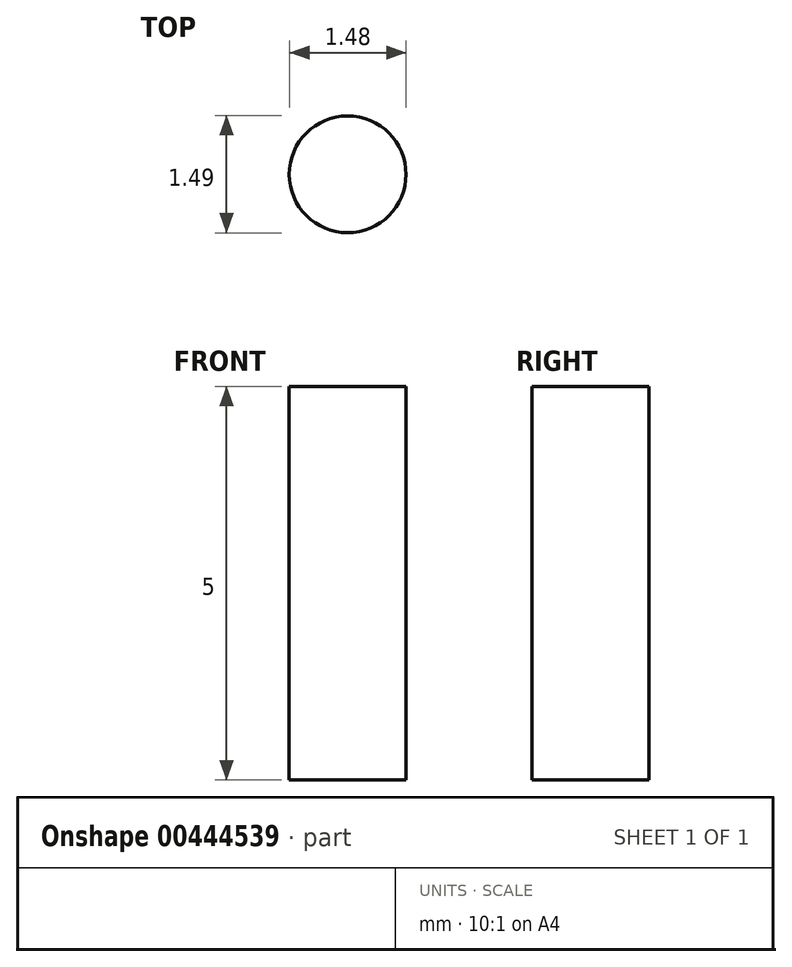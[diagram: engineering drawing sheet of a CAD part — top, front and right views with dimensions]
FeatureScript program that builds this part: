
annotation { "Feature Type Name" : "Feature", "Feature Type Description" : "" }
export const myFeature = defineFeature(function(context is Context, id is Id, definition is map)
    precondition{}
    {
        {
            var Q0;
            Q0=qCreatedBy(makeId("Top.planeOp"),FACE);
            var sketch = newSketch(context, id + "F0", { "sketchPlane" : qUnion([Q0])});
            skLineSegment(sketch, "E0.bottom", {"start": v(-4, 5) * mm, "end": v(4, 5) * mm});
            skLineSegment(sketch, "E0.top", {"start": v(-4, -5) * mm, "end": v(4, -5) * mm});
            skLineSegment(sketch, "E0.left", {"start": v(-5, 4) * mm, "end": v(-5, -4) * mm});
            skLineSegment(sketch, "E0.right", {"start": v(5, 4) * mm, "end": v(5, -4) * mm});
            skPoint(sketch, "E0.middle", {"position": v(0, 0) * mm});
            skPoint(sketch, "E1.visualSharp", {"position": v(-5, 5) * mm});
            skArc(sketch, "E1.filletArc", {"start": v(-4, 5) * mm, "mid": v(-4.7, 4.7) * mm, "end": v(-5, 4) * mm});
            skPoint(sketch, "E2.visualSharp", {"position": v(5, 5) * mm});
            skArc(sketch, "E2.filletArc", {"start": v(5, 4) * mm, "mid": v(4.7, 4.7) * mm, "end": v(4, 5) * mm});
            skPoint(sketch, "E3.visualSharp", {"position": v(5, -5) * mm});
            skArc(sketch, "E3.filletArc", {"start": v(4, -5) * mm, "mid": v(4.7, -4.7) * mm, "end": v(5, -4) * mm});
            skPoint(sketch, "E4.visualSharp", {"position": v(-5, -5) * mm});
            skArc(sketch, "E4.filletArc", {"start": v(-5, -4) * mm, "mid": v(-4.7, -4.7) * mm, "end": v(-4, -5) * mm});
            skSolve(sketch);
        }
        {
            var Q0;
            Q0 = qSketchRegion(id + "F0", true);
            extrude(context, id + "F1", {"entities" : qUnion([Q0]), "depth" : 5 * mm});
        }
        {
            var Q0;
            Q0=makeQuery(id+"F1.opExtrude","CAP_FACE",FACE,{"disambiguationData":[OSD([sQuery(id+"F0.wireOp",EDGE,"E0.bottom"),sQuery(id+"F0.wireOp",EDGE,"E0.top"),sQuery(id+"F0.wireOp",EDGE,"E0.left"),sQuery(id+"F0.wireOp",EDGE,"E0.right"),sQuery(id+"F0.wireOp",EDGE,"E1.filletArc"),sQuery(id+"F0.wireOp",EDGE,"E2.filletArc"),sQuery(id+"F0.wireOp",EDGE,"E3.filletArc"),sQuery(id+"F0.wireOp",EDGE,"E4.filletArc")])],"isStart":false});
            var sketch = newSketch(context, id + "F2", { "sketchPlane" : qUnion([Q0])});
            skCircle(sketch, "E5", {"center": v(-1.87, 1.9) * mm, "radius": 0.74 * mm});
            skCircle(sketch, "E6.MirrorC", {"center": v(1.87, 1.9) * mm, "radius": 0.74 * mm});
            skLineSegment(sketch, "E7.bottom", {"start": v(-3.1, -1.65) * mm, "end": v(3.1, -1.65) * mm});
            skLineSegment(sketch, "E7.top", {"start": v(-3.1, -2.84) * mm, "end": v(3.1, -2.84) * mm});
            skLineSegment(sketch, "E7.left", {"start": v(-3.1, -1.65) * mm, "end": v(-3.1, -2.84) * mm});
            skLineSegment(sketch, "E7.right", {"start": v(3.1, -1.65) * mm, "end": v(3.1, -2.84) * mm});
            skPoint(sketch, "E7.middle", {"position": v(0, -2.25) * mm});
            skSolve(sketch);
        }
        {
            var Q0;
            Q0=makeQuery(id+"F2.imprint","IMPRINT",FACE,{"disambiguationData":[TD([[makeQuery(id+"F2.imprint","IMPRINT",EDGE,{"derivedFrom":sQuery(id+"F2.wireOp",EDGE,"E5")}),1.0]])]});
            var Q1;
            Q1=makeQuery(id+"F2.imprint","IMPRINT",FACE,{"disambiguationData":[TD([[makeQuery(id+"F2.imprint","IMPRINT",EDGE,{"derivedFrom":sQuery(id+"F2.wireOp",EDGE,"E6.MirrorC")}),-1.0]])]});
            var Q2;
            Q2=makeQuery(id+"F2.imprint","IMPRINT",FACE,{"disambiguationData":[TD([[makeQuery(id+"F2.imprint","IMPRINT",EDGE,{"derivedFrom":sQuery(id+"F2.wireOp",EDGE,"E7.bottom")}),-1.0]])]});
            extrude(context, id + "F3", {"entities" : qUnion([Q0, Q1, Q2]), "operationType" : NewBodyOperationType.REMOVE, "oppositeDirection" : true, "depth" : 25 * mm});
        }
        {
            var Q0;
            Q0=makeQuery(id+"F1.opExtrude","CAP_FACE",FACE,{"disambiguationData":[OSD([sQuery(id+"F0.wireOp",EDGE,"E0.bottom"),sQuery(id+"F0.wireOp",EDGE,"E0.top"),sQuery(id+"F0.wireOp",EDGE,"E0.left"),sQuery(id+"F0.wireOp",EDGE,"E0.right"),sQuery(id+"F0.wireOp",EDGE,"E1.filletArc"),sQuery(id+"F0.wireOp",EDGE,"E2.filletArc"),sQuery(id+"F0.wireOp",EDGE,"E3.filletArc"),sQuery(id+"F0.wireOp",EDGE,"E4.filletArc")])],"isStart":false});
            var sketch = newSketch(context, id + "F4", { "sketchPlane" : qUnion([Q0])});
            skCircle(sketch, "E8", {"center": v(-4, 4) * mm, "radius": 0.45 * mm});
            skSolve(sketch);
        }
        {
            var Q0;
            Q0=makeQuery(id+"F4.imprint","IMPRINT",FACE,{"disambiguationData":[TD([[makeQuery(id+"F4.imprint","IMPRINT",EDGE,{"derivedFrom":sQuery(id+"F4.wireOp",EDGE,"E8")}),1.0]])]});
            var Q1;
            Q1=sQuery(id+"F4.wireOp",EDGE,"E8");
            extrude(context, id + "F5", {"entities" : qUnion([Q0]), "operationType" : NewBodyOperationType.REMOVE, "surfaceEntities" : qUnion([Q1]), "endBound" : BoundingType.THROUGH_ALL, "oppositeDirection" : true, "depth" : 25 * mm});
        }
    });
